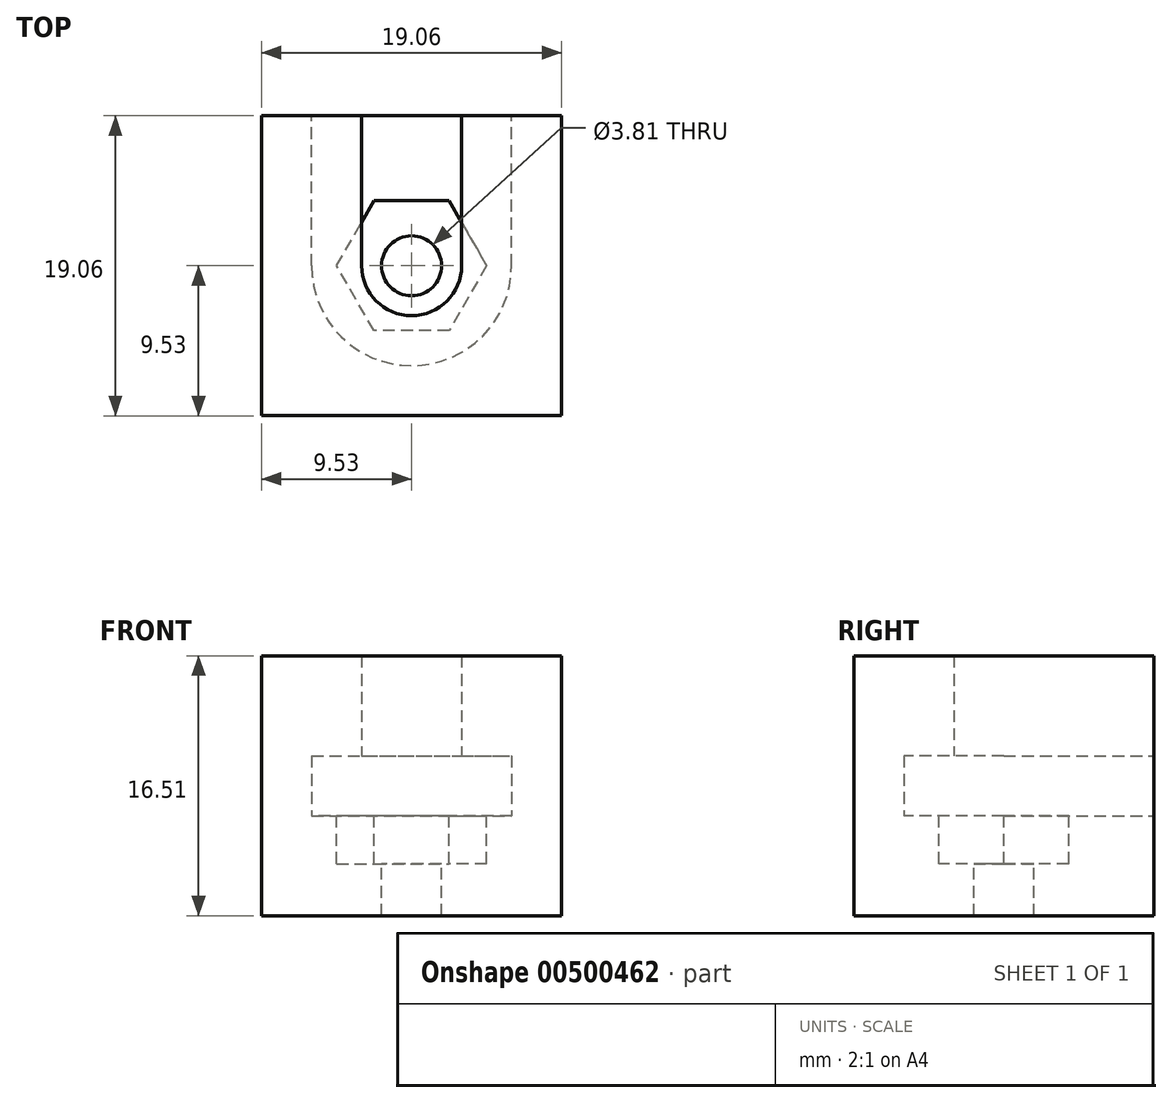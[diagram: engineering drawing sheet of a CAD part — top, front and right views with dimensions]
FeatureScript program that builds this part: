
annotation { "Feature Type Name" : "Feature", "Feature Type Description" : "" }
export const myFeature = defineFeature(function(context is Context, id is Id, definition is map)
    precondition{}
    {
        {
            var Q0;
            Q0=qCreatedBy(makeId("Top.planeOp"),FACE);
            var sketch = newSketch(context, id + "F0", { "sketchPlane" : qUnion([Q0])});
            skLineSegment(sketch, "E0.bottom", {"start": v(9.53, 9.53) * mm, "end": v(-9.53, 9.53) * mm});
            skLineSegment(sketch, "E0.top", {"start": v(9.53, -9.53) * mm, "end": v(-9.53, -9.53) * mm});
            skLineSegment(sketch, "E0.left", {"start": v(9.53, 9.53) * mm, "end": v(9.53, -9.53) * mm});
            skLineSegment(sketch, "E0.right", {"start": v(-9.53, 9.53) * mm, "end": v(-9.53, -9.53) * mm});
            skPoint(sketch, "E0.middle", {"position": v(0, 0) * mm});
            skSolve(sketch);
        }
        {
            var Q0;
            Q0=makeQuery(id+"F0.imprint","IMPRINT",FACE,{"disambiguationData":[TD([[makeQuery(id+"F0.imprint","IMPRINT",EDGE,{"derivedFrom":sQuery(id+"F0.wireOp",EDGE,"E0.bottom")}),1.0]])]});
            extrude(context, id + "F1", {"entities" : qUnion([Q0]), "oppositeDirection" : true, "depth" : 6.35 * mm});
        }
        {
            var Q0;
            Q0=makeQuery(id+"F1.opExtrude","CAP_FACE",FACE,{"disambiguationData":[OSD([sQuery(id+"F0.wireOp",EDGE,"E0.bottom"),sQuery(id+"F0.wireOp",EDGE,"E0.top"),sQuery(id+"F0.wireOp",EDGE,"E0.left"),sQuery(id+"F0.wireOp",EDGE,"E0.right")])],"isStart":true});
            var sketch = newSketch(context, id + "F2", { "sketchPlane" : qUnion([Q0])});
            skArc(sketch, "E1", {"start": v(-6.35, 0) * mm, "mid": v(0, -6.35) * mm, "end": v(6.35, 0) * mm});
            skLineSegment(sketch, "E2", {"start": v(6.35, 0) * mm, "end": v(6.35, 9.52) * mm});
            skPoint(sketch, "E2.startSnap0", {"position": v(9.53, 0) * mm});
            skLineSegment(sketch, "E3", {"start": v(-6.35, 0) * mm, "end": v(-6.35, 9.53) * mm});
            skLineSegment(sketch, "E4.bottom", {"start": v(-9.53, 9.53) * mm, "end": v(-6.35, 9.53) * mm});
            skLineSegment(sketch, "E4.top", {"start": v(-9.53, -9.53) * mm, "end": v(9.53, -9.53) * mm});
            skLineSegment(sketch, "E4.left", {"start": v(-9.53, 9.53) * mm, "end": v(-9.53, -9.53) * mm});
            skLineSegment(sketch, "E4.right", {"start": v(9.53, 9.53) * mm, "end": v(9.53, -9.53) * mm});
            skLineSegment(sketch, "E5.trimOffspring", {"start": v(6.35, 9.53) * mm, "end": v(9.53, 9.53) * mm});
            skSolve(sketch);
        }
        {
            var Q0;
            Q0=makeQuery(id+"F2.imprint","IMPRINT",FACE,{"disambiguationData":[TD([[makeQuery(id+"F2.imprint","IMPRINT",EDGE,{"derivedFrom":sQuery(id+"F2.wireOp",EDGE,"E1")}),-1.0]])]});
            extrude(context, id + "F3", {"entities" : qUnion([Q0]), "operationType" : NewBodyOperationType.ADD, "depth" : 3.8 * mm});
        }
        {
            var Q0;
            Q0=makeQuery(id+"F3.opExtrude","CAP_FACE",FACE,{"disambiguationData":[OSD([sQuery(id+"F2.wireOp",EDGE,"E1"),sQuery(id+"F2.wireOp",EDGE,"E2"),sQuery(id+"F2.wireOp",EDGE,"E3"),sQuery(id+"F2.wireOp",EDGE,"E4.bottom"),sQuery(id+"F2.wireOp",EDGE,"E4.top"),sQuery(id+"F2.wireOp",EDGE,"E4.left"),sQuery(id+"F2.wireOp",EDGE,"E4.right"),sQuery(id+"F2.wireOp",EDGE,"E5.trimOffspring")])],"isStart":false});
            var sketch = newSketch(context, id + "F4", { "sketchPlane" : qUnion([Q0])});
            skLineSegment(sketch, "E6.bottom", {"start": v(-9.53, 9.53) * mm, "end": v(-3.18, 9.53) * mm});
            skLineSegment(sketch, "E6.top", {"start": v(-9.53, -9.53) * mm, "end": v(9.53, -9.53) * mm});
            skLineSegment(sketch, "E6.left", {"start": v(-9.53, 9.53) * mm, "end": v(-9.53, -9.53) * mm});
            skLineSegment(sketch, "E6.right", {"start": v(9.53, 9.53) * mm, "end": v(9.53, -9.53) * mm});
            skArc(sketch, "E7", {"start": v(-3.18, 0) * mm, "mid": v(0, -3.18) * mm, "end": v(3.18, 0) * mm});
            skLineSegment(sketch, "E8", {"start": v(-3.18, 0) * mm, "end": v(-3.18, 9.53) * mm});
            skLineSegment(sketch, "E9", {"start": v(3.18, 0) * mm, "end": v(3.18, 9.53) * mm});
            skLineSegment(sketch, "E10.trimOffspring", {"start": v(3.18, 9.53) * mm, "end": v(9.53, 9.53) * mm});
            skSolve(sketch);
        }
        {
            var Q0;
            Q0 = qSketchRegion(id + "F4", true);
            extrude(context, id + "F5", {"entities" : qUnion([Q0]), "operationType" : NewBodyOperationType.ADD, "depth" : 6.35 * mm});
        }
        {
            var Q0;
            Q0=makeQuery(id+"F1.opExtrude","CAP_FACE",FACE,{"disambiguationData":[OSD([sQuery(id+"F0.wireOp",EDGE,"E0.bottom"),sQuery(id+"F0.wireOp",EDGE,"E0.top"),sQuery(id+"F0.wireOp",EDGE,"E0.left"),sQuery(id+"F0.wireOp",EDGE,"E0.right")])],"isStart":true});
            var sketch = newSketch(context, id + "F6", { "sketchPlane" : qUnion([Q0])});
            skCircle(sketch, "E11.cCircle", {"center": v(0, 0) * mm, "radius": 4.13 * mm, "construction": true});
            skLineSegment(sketch, "E11.0", {"start": v(4.77, 0) * mm, "end": v(2.38, -4.13) * mm});
            skLineSegment(sketch, "E11.1", {"start": v(2.38, -4.13) * mm, "end": v(-2.38, -4.13) * mm});
            skLineSegment(sketch, "E11.2", {"start": v(-2.38, -4.13) * mm, "end": v(-4.77, 0) * mm});
            skLineSegment(sketch, "E11.3", {"start": v(-4.77, 0) * mm, "end": v(-2.38, 4.13) * mm});
            skLineSegment(sketch, "E11.4", {"start": v(-2.38, 4.13) * mm, "end": v(2.38, 4.13) * mm});
            skLineSegment(sketch, "E11.5", {"start": v(2.38, 4.13) * mm, "end": v(4.77, 0) * mm});
            skPoint(sketch, "E11.0.midPoint", {"position": v(3.57, -2.06) * mm});
            skSolve(sketch);
        }
        {
            var Q0;
            Q0=makeQuery(id+"F6.imprint","IMPRINT",FACE,{"disambiguationData":[TD([[makeQuery(id+"F6.imprint","IMPRINT",EDGE,{"derivedFrom":sQuery(id+"F6.wireOp",EDGE,"E11.0")}),-1.0]])]});
            extrude(context, id + "F7", {"entities" : qUnion([Q0]), "operationType" : NewBodyOperationType.REMOVE, "oppositeDirection" : true, "depth" : 3.05 * mm});
        }
        {
            var Q0;
            Q0=makeQuery(id+"F7.boolean.opBoolean","COPY",FACE,{"derivedFrom":makeQuery(id+"F7.opExtrude","CAP_FACE",FACE,{"disambiguationData":[OSD([sQuery(id+"F6.wireOp",EDGE,"E11.0"),sQuery(id+"F6.wireOp",EDGE,"E11.1"),sQuery(id+"F6.wireOp",EDGE,"E11.2"),sQuery(id+"F6.wireOp",EDGE,"E11.3"),sQuery(id+"F6.wireOp",EDGE,"E11.4"),sQuery(id+"F6.wireOp",EDGE,"E11.5")])],"isStart":false})});
            var sketch = newSketch(context, id + "F8", { "sketchPlane" : qUnion([Q0])});
            skCircle(sketch, "E12", {"center": v(0, 0) * mm, "radius": 1.9 * mm});
            skSolve(sketch);
        }
        {
            var Q0;
            Q0=makeQuery(id+"F8.imprint","IMPRINT",FACE,{"disambiguationData":[TD([[makeQuery(id+"F8.imprint","IMPRINT",EDGE,{"derivedFrom":sQuery(id+"F8.wireOp",EDGE,"E12")}),1.0]])]});
            extrude(context, id + "F9", {"entities" : qUnion([Q0]), "operationType" : NewBodyOperationType.REMOVE, "endBound" : BoundingType.THROUGH_ALL, "oppositeDirection" : true, "depth" : 25.4 * mm});
        }
    });
